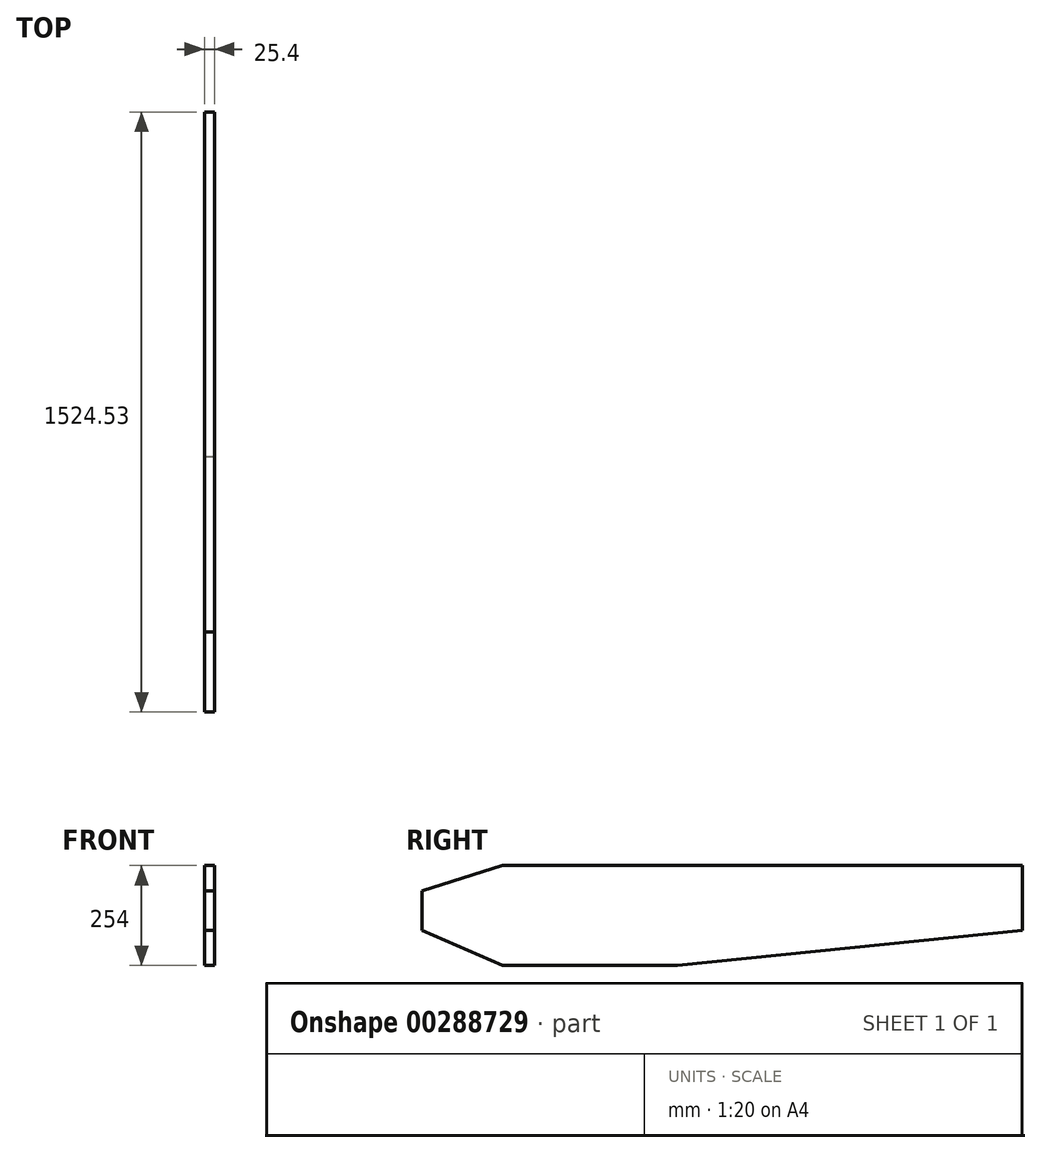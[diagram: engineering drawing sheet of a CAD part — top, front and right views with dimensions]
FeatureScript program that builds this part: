
annotation { "Feature Type Name" : "Feature", "Feature Type Description" : "" }
export const myFeature = defineFeature(function(context is Context, id is Id, definition is map)
    precondition{}
    {
        {
            var Q0;
            Q0=qCreatedBy(makeId("Right.planeOp"),FACE);
            var sketch = newSketch(context, id + "F0", { "sketchPlane" : qUnion([Q0])});
            skLineSegment(sketch, "E0.0.1", {"start": v(66.3, 113.45) * mm, "end": v(-378.27, 113.45) * mm});
            skLineSegment(sketch, "E0.0.3", {"start": v(-378.27, -140.55) * mm, "end": v(66.23, -140.55) * mm});
            skLineSegment(sketch, "E1.0.0", {"start": v(942.6, 113.45) * mm, "end": v(66.3, 113.45) * mm});
            skLineSegment(sketch, "E1.0.2", {"start": v(66.23, -140.55) * mm, "end": v(942.6, -51.65) * mm});
            skLineSegment(sketch, "E1.0.3", {"start": v(942.6, -51.65) * mm, "end": v(942.6, 113.45) * mm});
            skLineSegment(sketch, "E2.0.0", {"start": v(-581.93, -51.65) * mm, "end": v(-378.27, -140.55) * mm});
            skLineSegment(sketch, "E2.0.2", {"start": v(-378.27, 113.45) * mm, "end": v(-581.93, 49.47) * mm});
            skLineSegment(sketch, "E2.0.3", {"start": v(-581.93, 49.47) * mm, "end": v(-581.93, -51.65) * mm});
            skSolve(sketch);
        }
        {
            var Q0;
            Q0 = qSketchRegion(id + "F0", true);
            var Q1;
            Q1 = qConstructionFilter(qBodyType(qCreatedBy(id + "F0" ,EDGE), BodyType.WIRE), ConstructionObject.NO);
            extrude(context, id + "F1", {"entities" : qUnion([Q0]), "surfaceEntities" : qUnion([Q1]), "endBound" : BoundingType.SYMMETRIC, "depth" : 25.4 * mm});
        }
    });
